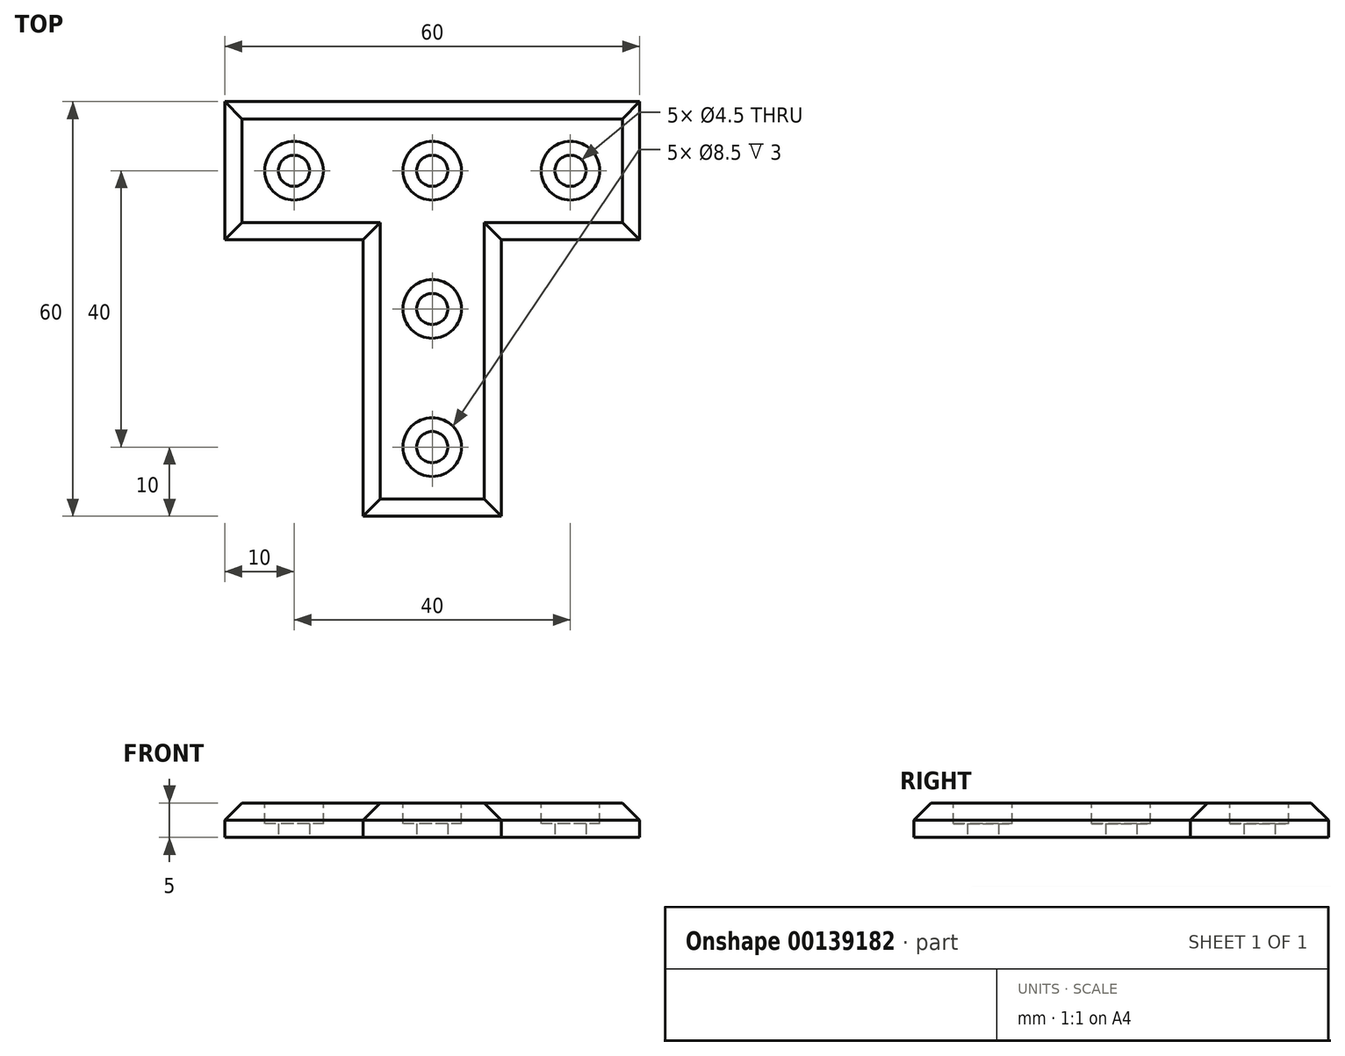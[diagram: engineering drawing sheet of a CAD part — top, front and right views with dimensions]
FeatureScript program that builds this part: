
annotation { "Feature Type Name" : "Feature", "Feature Type Description" : "" }
export const myFeature = defineFeature(function(context is Context, id is Id, definition is map)
    precondition{}
    {
        {
            var Q0;
            Q0=qCreatedBy(makeId("Top.planeOp"),FACE);
            var sketch = newSketch(context, id + "F0", { "sketchPlane" : qUnion([Q0])});
            skLineSegment(sketch, "E0", {"start": v(0, -50) * mm, "end": v(10, -50) * mm});
            skLineSegment(sketch, "E1", {"start": v(10, -50) * mm, "end": v(10, -10) * mm});
            skLineSegment(sketch, "E2", {"start": v(10, -10) * mm, "end": v(50, -10) * mm});
            skLineSegment(sketch, "E3", {"start": v(50, -10) * mm, "end": v(50, 10) * mm});
            skLineSegment(sketch, "E4", {"start": v(50, 10) * mm, "end": v(0, 10) * mm});
            skLineSegment(sketch, "E5.MirrorCS", {"start": v(-10, -50) * mm, "end": v(-10, -10) * mm});
            skLineSegment(sketch, "E6.MirrorCS", {"start": v(0, -50) * mm, "end": v(-10, -50) * mm});
            skLineSegment(sketch, "E7.MirrorCS", {"start": v(-50, -10) * mm, "end": v(-50, 10) * mm});
            skLineSegment(sketch, "E8.MirrorCS", {"start": v(-10, -10) * mm, "end": v(-50, -10) * mm});
            skLineSegment(sketch, "E9.MirrorCS", {"start": v(-50, 10) * mm, "end": v(0, 10) * mm});
            skCircle(sketch, "E10", {"center": v(0, 0) * mm, "radius": 2.25 * mm});
            skCircle(sketch, "E11", {"center": v(20, 0) * mm, "radius": 2.25 * mm});
            skCircle(sketch, "E12", {"center": v(40, 0) * mm, "radius": 2.25 * mm});
            skCircle(sketch, "E13", {"center": v(0, -20) * mm, "radius": 2.25 * mm});
            skCircle(sketch, "E14", {"center": v(0, -40) * mm, "radius": 2.25 * mm});
            skCircle(sketch, "E15.MirrorC", {"center": v(-40, 0) * mm, "radius": 2.25 * mm});
            skCircle(sketch, "E16.MirrorC", {"center": v(-20, 0) * mm, "radius": 2.25 * mm});
            skLineSegment(sketch, "E17", {"start": v(-30, -10) * mm, "end": v(-30, 10) * mm});
            skLineSegment(sketch, "E18", {"start": v(30, -10) * mm, "end": v(30, 10) * mm});
            skSolve(sketch);
        }
        {
            var Q0;
            Q0=makeQuery(id+"F0.imprint","IMPRINT",FACE,{"disambiguationData":[TD([[makeQuery(id+"F0.imprint","IMPRINT",EDGE,{"derivedFrom":sQuery(id+"F0.wireOp",EDGE,"E0")}),1.0]])]});
            extrude(context, id + "F1", {"entities" : qUnion([Q0]), "depth" : 5 * mm});
        }
        {
            var Q0;
            Q0=makeQuery(id+"F1.opExtrude","CAP_EDGE",EDGE,{"disambiguationData":[OSD([sQuery(id+"F0.wireOp",EDGE,"E0"),sQuery(id+"F0.wireOp",EDGE,"E6.MirrorCS")])],"isStart":false});
            var Q1;
            Q1=makeQuery(id+"F1.opExtrude","CAP_EDGE",EDGE,{"disambiguationData":[OSD([sQuery(id+"F0.wireOp",EDGE,"E1")])],"isStart":false});
            var Q2;
            Q2=makeQuery(id+"F1.opExtrude","CAP_EDGE",EDGE,{"disambiguationData":[OSD([sQuery(id+"F0.wireOp",EDGE,"E2")])],"isStart":false});
            var Q3;
            Q3=makeQuery(id+"F1.opExtrude","CAP_EDGE",EDGE,{"disambiguationData":[OSD([sQuery(id+"F0.wireOp",EDGE,"E3")])],"isStart":false});
            var Q4;
            Q4=makeQuery(id+"F1.opExtrude","CAP_EDGE",EDGE,{"disambiguationData":[OSD([sQuery(id+"F0.wireOp",EDGE,"E4"),sQuery(id+"F0.wireOp",EDGE,"E9.MirrorCS")])],"isStart":false});
            var Q5;
            Q5=makeQuery(id+"F1.opExtrude","CAP_EDGE",EDGE,{"disambiguationData":[OSD([sQuery(id+"F0.wireOp",EDGE,"E7.MirrorCS")])],"isStart":false});
            var Q6;
            Q6=makeQuery(id+"F1.opExtrude","CAP_EDGE",EDGE,{"disambiguationData":[OSD([sQuery(id+"F0.wireOp",EDGE,"E8.MirrorCS")])],"isStart":false});
            var Q7;
            Q7=makeQuery(id+"F1.opExtrude","CAP_EDGE",EDGE,{"disambiguationData":[OSD([sQuery(id+"F0.wireOp",EDGE,"E5.MirrorCS")])],"isStart":false});
            var Q8;
            Q8=makeQuery(id+"F1.opExtrude","CAP_EDGE",EDGE,{"disambiguationData":[OSD([sQuery(id+"F0.wireOp",EDGE,"E17")])],"isStart":false});
            var Q9;
            Q9=makeQuery(id+"F1.opExtrude","CAP_EDGE",EDGE,{"disambiguationData":[OSD([sQuery(id+"F0.wireOp",EDGE,"E18")])],"isStart":false});
            chamfer(context, id + "F2", {"entities" : qUnion([Q0, Q1, Q2, Q3, Q4, Q5, Q6, Q7, Q8, Q9]), "width" : 2.5 * mm, "tangentPropagation" : true});
        }
        {
            var Q0;
            Q0=makeQuery(id+"F1.opExtrude","CAP_FACE",FACE,{"disambiguationData":[OSD([sQuery(id+"F0.wireOp",EDGE,"E0"),sQuery(id+"F0.wireOp",EDGE,"E1"),sQuery(id+"F0.wireOp",EDGE,"E2"),sQuery(id+"F0.wireOp",EDGE,"E4"),sQuery(id+"F0.wireOp",EDGE,"E5.MirrorCS"),sQuery(id+"F0.wireOp",EDGE,"E6.MirrorCS"),sQuery(id+"F0.wireOp",EDGE,"E8.MirrorCS"),sQuery(id+"F0.wireOp",EDGE,"E9.MirrorCS"),sQuery(id+"F0.wireOp",EDGE,"E10"),sQuery(id+"F0.wireOp",EDGE,"E11"),sQuery(id+"F0.wireOp",EDGE,"E13"),sQuery(id+"F0.wireOp",EDGE,"E14"),sQuery(id+"F0.wireOp",EDGE,"E16.MirrorC"),sQuery(id+"F0.wireOp",EDGE,"E17"),sQuery(id+"F0.wireOp",EDGE,"E18")])],"isStart":false});
            var sketch = newSketch(context, id + "F3", { "sketchPlane" : qUnion([Q0])});
            skCircle(sketch, "E19", {"center": v(0, -40) * mm, "radius": 4.25 * mm});
            skCircle(sketch, "E20", {"center": v(0, -20) * mm, "radius": 4.25 * mm});
            skCircle(sketch, "E21", {"center": v(-20, 0) * mm, "radius": 4.25 * mm});
            skCircle(sketch, "E22", {"center": v(0, 0) * mm, "radius": 4.25 * mm});
            skCircle(sketch, "E23", {"center": v(20, 0) * mm, "radius": 4.25 * mm});
            skSolve(sketch);
        }
        {
            var Q0;
            Q0=makeQuery(id+"F3.imprint","IMPRINT",FACE,{"disambiguationData":[TD([[makeQuery(id+"F3.imprint","IMPRINT",EDGE,{"derivedFrom":sQuery(id+"F3.wireOp",EDGE,"E21")}),1.0]])]});
            var Q1;
            Q1=makeQuery(id+"F3.imprint","IMPRINT",FACE,{"disambiguationData":[TD([[makeQuery(id+"F3.imprint","IMPRINT",EDGE,{"derivedFrom":sQuery(id+"F3.wireOp",EDGE,"E22")}),1.0]])]});
            var Q2;
            Q2=makeQuery(id+"F3.imprint","IMPRINT",FACE,{"disambiguationData":[TD([[makeQuery(id+"F3.imprint","IMPRINT",EDGE,{"derivedFrom":sQuery(id+"F3.wireOp",EDGE,"E23")}),1.0]])]});
            var Q3;
            Q3=makeQuery(id+"F3.imprint","IMPRINT",FACE,{"disambiguationData":[TD([[makeQuery(id+"F3.imprint","IMPRINT",EDGE,{"derivedFrom":sQuery(id+"F3.wireOp",EDGE,"E20")}),1.0]])]});
            var Q4;
            Q4=makeQuery(id+"F3.imprint","IMPRINT",FACE,{"disambiguationData":[TD([[makeQuery(id+"F3.imprint","IMPRINT",EDGE,{"derivedFrom":sQuery(id+"F3.wireOp",EDGE,"E19")}),1.0]])]});
            extrude(context, id + "F4", {"entities" : qUnion([Q0, Q1, Q2, Q3, Q4]), "operationType" : NewBodyOperationType.REMOVE, "oppositeDirection" : true, "depth" : 3 * mm});
        }
    });
